# Revit family: 706660001_Dispensador de Jabón de Mesón
name_source: partatom
category: Generic Models
units: mm (PartAtom-declared; Revit-internal decimal feet)

## family parameters
Can host rebar = No
Cut with Voids When Loaded = No
Host = Face
OmniClass Number = 23.40.20.21
OmniClass Title = Toilet and Bath Specialties
Part Type = Normal
Room Calculation Point = No
Round Connector Dimension = Use Diameter
Shared = No

## types (1)
- 706660001_Dispensador de Jabón de Mesón
    Alto = 457 mm  [stored 1.49934 ft]
    Ancho = 90 mm  [stored 0.295276 ft]
    Capacidad de carga = Jabón líquido 1 lt. - 0,26 gl.
    Creado por = IDD
    Default Elevation = 1219 mm
    Dimensiones generales producto (H * W * D) = 456,5 x 195 x 90 mm.
18 x 7,7 x 3,5 pulg.
    Fabricante = Corona
    Fecha de creación = 30/07/2020
    Garantía = 1 año
    Peso Bruto aprox = 600 gr. - 1,2 lbs.
    Peso Neto aprox = 500 gr. - 1 lbs.
    Profundidad = 195 mm
    Referencia = 706660001
    URL = https://corona.co

note: [stored X ft] marks values corroborated as IEEE doubles in the binary element streams (Revit-internal decimal feet)

## geometry (parser evidence)
native form markers: Sweep x6
no freeform markers — native parametric forms only
